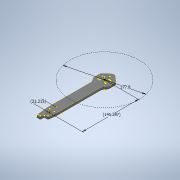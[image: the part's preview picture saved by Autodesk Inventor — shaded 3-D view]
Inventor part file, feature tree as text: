
AUTODESK INVENTOR PART (.ipt)
format: ipt  version: 2020 (Build 240168000, 168)  size: 201,728 bytes
history: native  units: in
note: dims shown in document units (in); Inventor stores cm internally (conversion verified against a paired STEP export)
features: sketch x2, projected_geometry x1
ambient origin geometry x8: Origin, YZ Plane, XZ Plane, XY Plane, X Axis, Y Axis, Z Axis, Center Point
bodies: Solid2 (feature_tree), Solid1 (feature_tree)
feature tree (3):
  sketch  "Sketch1"  dims[d0=7.0in]
  sketch  "Sketch2"  dims[d1=5.72in d2=0.8352in]
  projected_geometry  "Projected Loop1"
